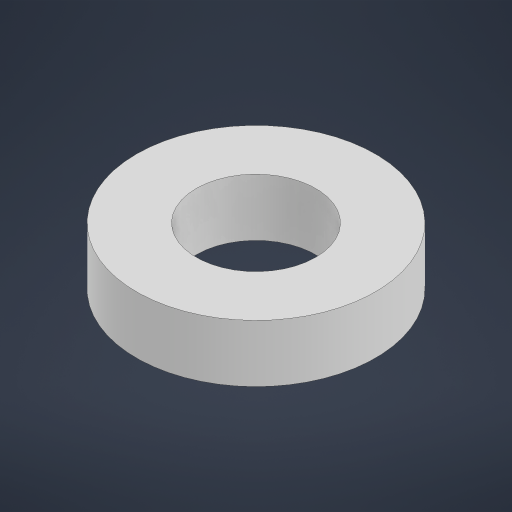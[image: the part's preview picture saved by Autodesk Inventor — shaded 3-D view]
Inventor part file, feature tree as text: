
AUTODESK INVENTOR PART (.ipt)
format: ipt  version: 2024 (Build 280153000, 153)  size: 159,232 bytes
history: native  units: mm
features: other x1, extrude x1, sketch x1
ambient origin geometry x8: Origin, YZ Plane, XZ Plane, XY Plane, X Axis, Y Axis, Z Axis, Center Point
bodies: Body1 (feature_tree)
feature tree (3):
  other  "솔리드1"
  extrude  "돌출1"  Depth=10.0mm
  sketch  "스케치1"
